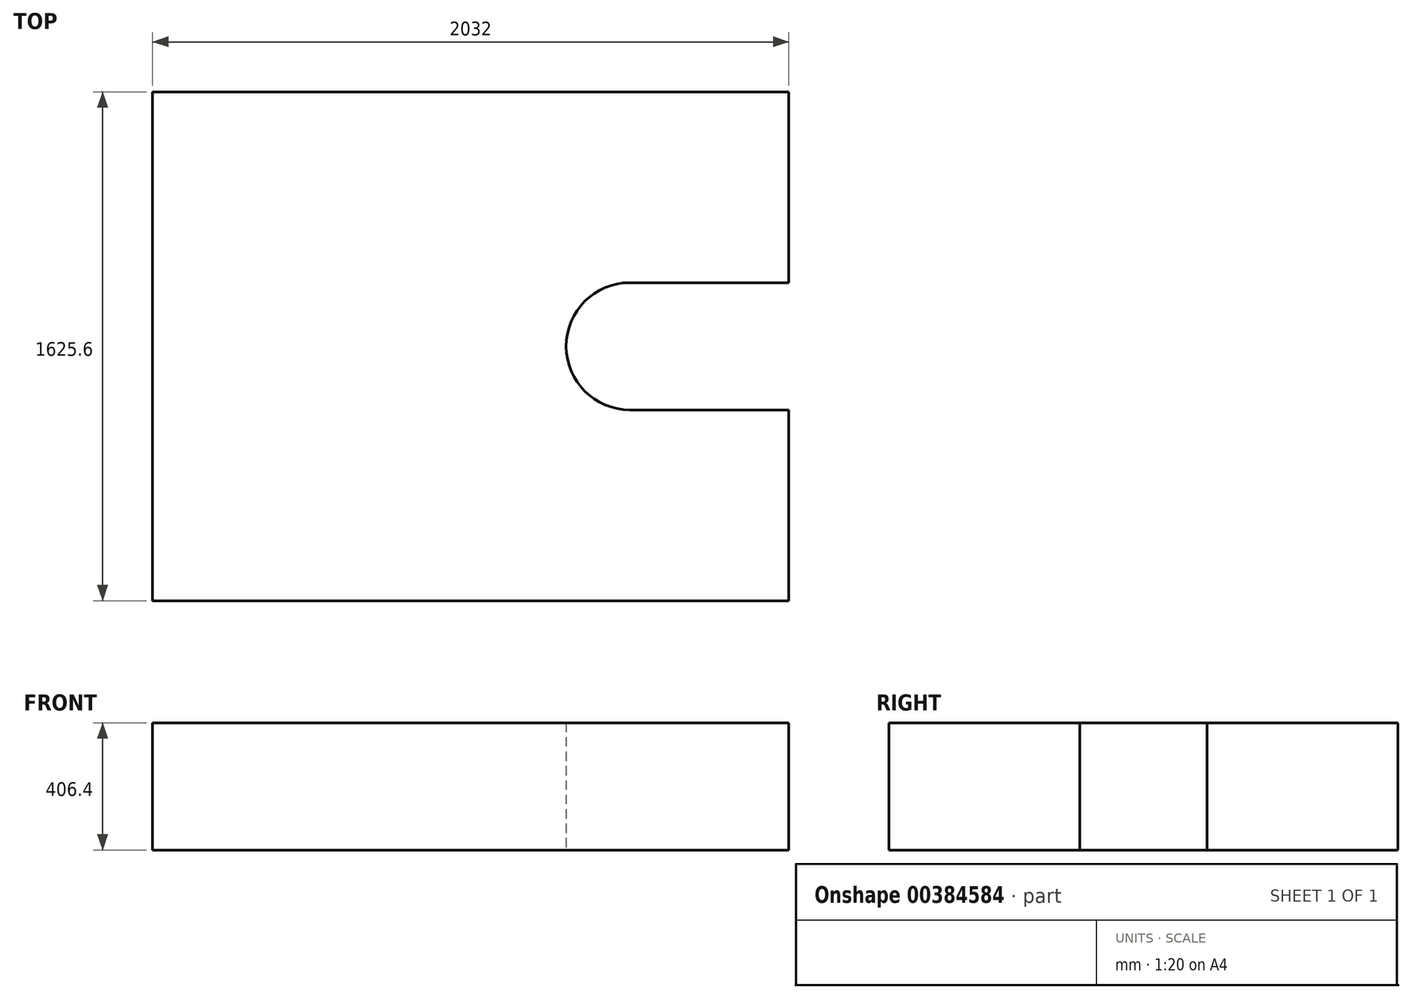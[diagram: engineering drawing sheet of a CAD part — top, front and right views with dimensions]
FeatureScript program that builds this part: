
annotation { "Feature Type Name" : "Feature", "Feature Type Description" : "" }
export const myFeature = defineFeature(function(context is Context, id is Id, definition is map)
    precondition{}
    {
        {
            var Q0;
            Q0=qCreatedBy(makeId("Top.planeOp"),FACE);
            var sketch = newSketch(context, id + "F0", { "sketchPlane" : qUnion([Q0])});
            skLineSegment(sketch, "E0", {"start": v(-143.4, 76.3) * mm, "end": v(1888.6, 76.3) * mm});
            skLineSegment(sketch, "E1", {"start": v(1888.6, 76.3) * mm, "end": v(1888.6, -533.3) * mm});
            skLineSegment(sketch, "E2", {"start": v(1888.6, -533.3) * mm, "end": v(1380.6, -533.3) * mm});
            skLineSegment(sketch, "E3", {"start": v(1380.6, -939.7) * mm, "end": v(1888.6, -939.7) * mm});
            skLineSegment(sketch, "E4", {"start": v(1888.6, -939.7) * mm, "end": v(1888.6, -1549.3) * mm});
            skLineSegment(sketch, "E5", {"start": v(1888.6, -1549.3) * mm, "end": v(-143.4, -1549.3) * mm});
            skLineSegment(sketch, "E6", {"start": v(-143.4, -1549.3) * mm, "end": v(-143.4, 76.3) * mm});
            skArc(sketch, "E7", {"start": v(1380.6, -533.3) * mm, "mid": v(1177.4, -736.5) * mm, "end": v(1380.6, -939.7) * mm});
            skSolve(sketch);
        }
        {
            var Q0;
            Q0=makeQuery(id+"F0.imprint","IMPRINT",FACE,{"disambiguationData":[TD([[makeQuery(id+"F0.imprint","IMPRINT",EDGE,{"derivedFrom":sQuery(id+"F0.wireOp",EDGE,"E0")}),-1.0]])]});
            extrude(context, id + "F1", {"entities" : qUnion([Q0]), "depth" : 406.4 * mm});
        }
    });
